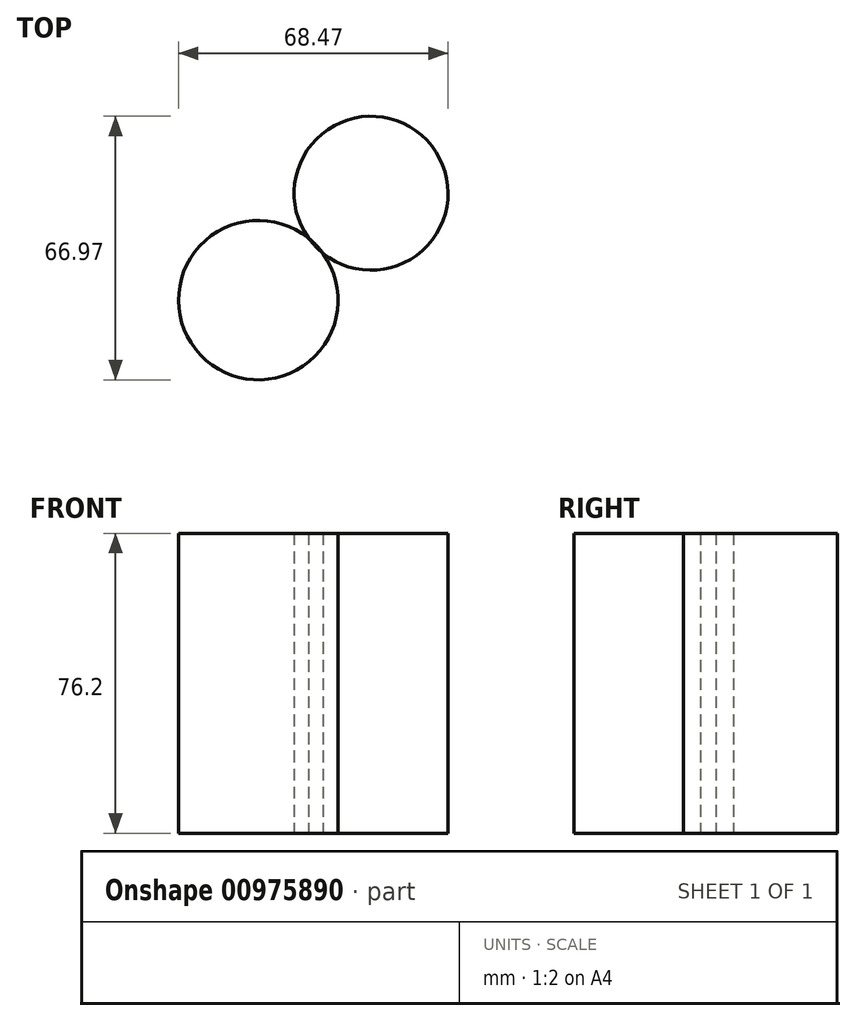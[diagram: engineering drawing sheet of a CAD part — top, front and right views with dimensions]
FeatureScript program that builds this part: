
annotation { "Feature Type Name" : "Feature", "Feature Type Description" : "" }
export const myFeature = defineFeature(function(context is Context, id is Id, definition is map)
    precondition{}
    {
        {
            var Q0;
            Q0=qCreatedBy(makeId("Top.planeOp"),FACE);
            var sketch = newSketch(context, id + "F0", { "sketchPlane" : qUnion([Q0])});
            skCircle(sketch, "E0", {"center": v(15.9, 11.4) * mm, "radius": 19.56 * mm});
            skCircle(sketch, "E1", {"center": v(-12.75, -15.75) * mm, "radius": 20.26 * mm});
            skSolve(sketch);
        }
        {
            var Q0;
            {var subQ0=sQuery(id+"F0.wireOp",EDGE,"E1");var subQ1=sQuery(id+"F0.wireOp",EDGE,"E0");var subQ2=makeQuery(id+"F0.imprint","INTERSECT",VERTEX,{"disambiguationData":[OD(0.0)],"derivedFrom":[subQ1,subQ0]});Q0=makeQuery(id+"F0.imprint","IMPRINT",FACE,{"disambiguationData":[TD([[makeQuery(id+"F0.imprint","IMPRINT",EDGE,{"disambiguationData":[TD([[subQ2,-1.0]])],"derivedFrom":subQ1}),-1.0]])]});}
            var Q1;
            {var subQ0=sQuery(id+"F0.wireOp",EDGE,"E1");var subQ1=sQuery(id+"F0.wireOp",EDGE,"E0");var subQ2=makeQuery(id+"F0.imprint","INTERSECT",VERTEX,{"disambiguationData":[OD(0.0)],"derivedFrom":[subQ1,subQ0]});Q1=makeQuery(id+"F0.imprint","IMPRINT",FACE,{"disambiguationData":[TD([[makeQuery(id+"F0.imprint","IMPRINT",EDGE,{"disambiguationData":[TD([[subQ2,1.0]])],"derivedFrom":subQ1}),1.0]])]});}
            extrude(context, id + "F1", {"entities" : qUnion([Q0, Q1]), "depth" : 76.2 * mm, "offsetDistance" : 25.4 * mm});
        }
    });
